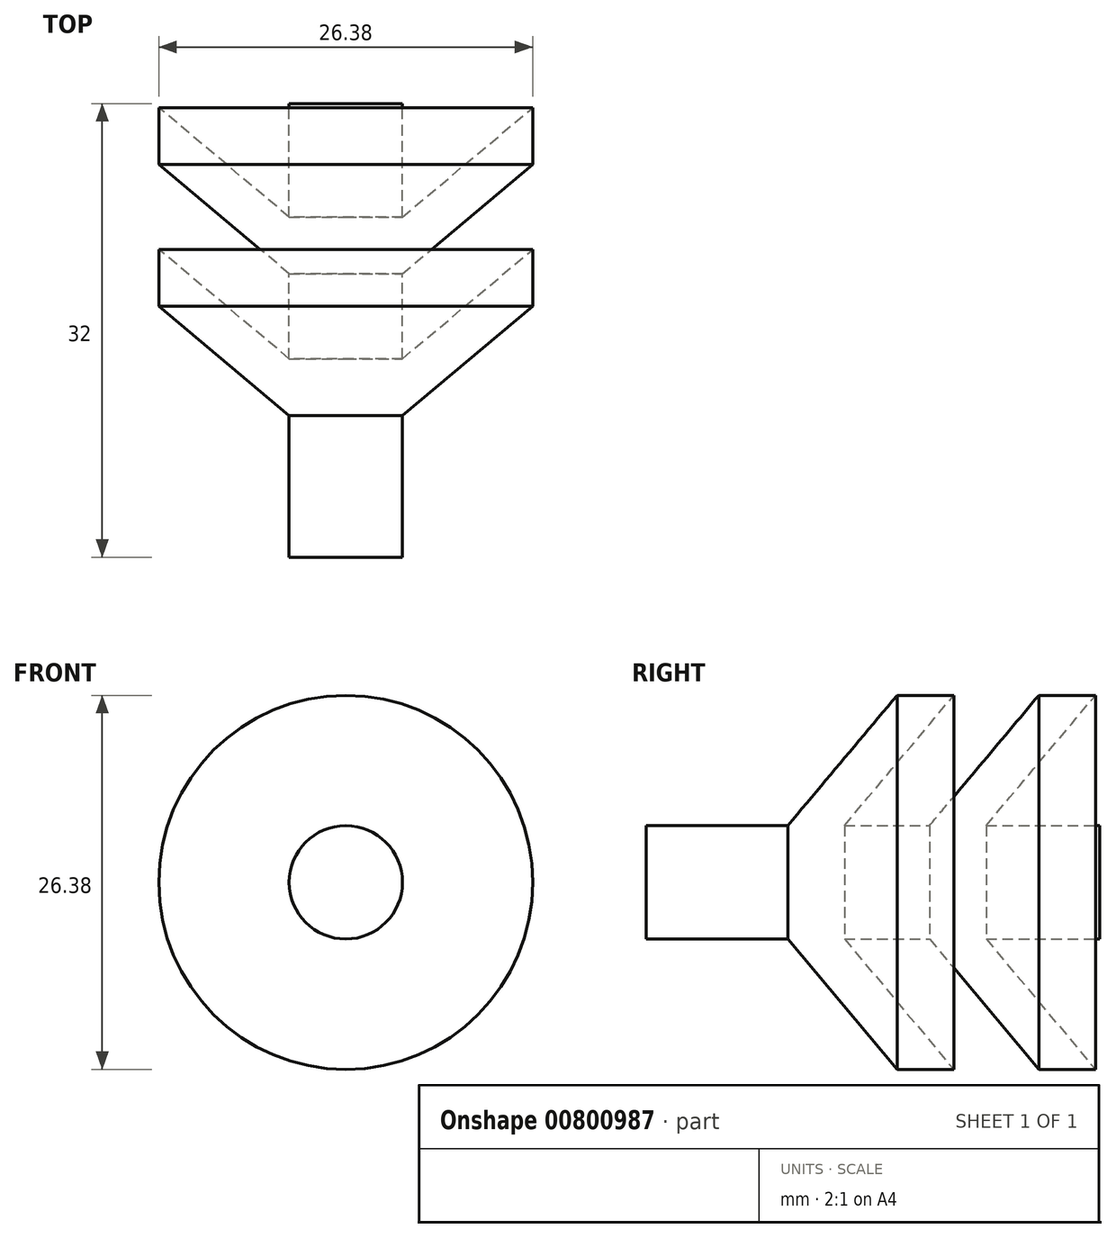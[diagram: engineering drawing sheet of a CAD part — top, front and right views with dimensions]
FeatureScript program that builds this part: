
annotation { "Feature Type Name" : "Feature", "Feature Type Description" : "" }
export const myFeature = defineFeature(function(context is Context, id is Id, definition is map)
    precondition{}
    {
        {
            var Q0;
            Q0=qCreatedBy(makeId("Top.planeOp"),FACE);
            var sketch = newSketch(context, id + "F0", { "sketchPlane" : qUnion([Q0])});
            skLineSegment(sketch, "E0", {"start": v(0, 0) * mm, "end": v(0, -32) * mm});
            skLineSegment(sketch, "E1", {"start": v(0, -32) * mm, "end": v(4, -32) * mm});
            skLineSegment(sketch, "E2", {"start": v(4, -32) * mm, "end": v(4, -22) * mm});
            skLineSegment(sketch, "E3", {"start": v(4, -22) * mm, "end": v(13.2, -14.29) * mm});
            skLineSegment(sketch, "E4", {"start": v(13.2, -14.29) * mm, "end": v(13.2, -10.29) * mm});
            skLineSegment(sketch, "E5", {"start": v(13.2, -10.29) * mm, "end": v(4, -18) * mm});
            skLineSegment(sketch, "E6", {"start": v(4, -18) * mm, "end": v(4, -12) * mm});
            skLineSegment(sketch, "E7", {"start": v(4, -12) * mm, "end": v(13.2, -4.29) * mm});
            skLineSegment(sketch, "E8", {"start": v(4, -8) * mm, "end": v(4, 0) * mm});
            skLineSegment(sketch, "E9", {"start": v(4, 0) * mm, "end": v(0, 0) * mm});
            skLineSegment(sketch, "E10", {"start": v(13.2, -4.29) * mm, "end": v(13.2, -0.29) * mm});
            skLineSegment(sketch, "E11", {"start": v(13.2, -0.29) * mm, "end": v(4, -8) * mm});
            skSolve(sketch);
        }
        {
            var Q0;
            Q0=makeQuery(id+"F0.imprint","IMPRINT",FACE,{"disambiguationData":[TD([[makeQuery(id+"F0.imprint","IMPRINT",EDGE,{"derivedFrom":sQuery(id+"F0.wireOp",EDGE,"E0")}),1.0]])]});
            var Q1;
            Q1=sQuery(id+"F0.wireOp",EDGE,"E0");
            revolve(context, id + "F1", {"surfaceOperationType" : NewSurfaceOperationType.NEW, "entities" : qUnion([Q0]), "axis" : qUnion([Q1]), "revolveType" : RevolveType.FULL});
        }
    });
